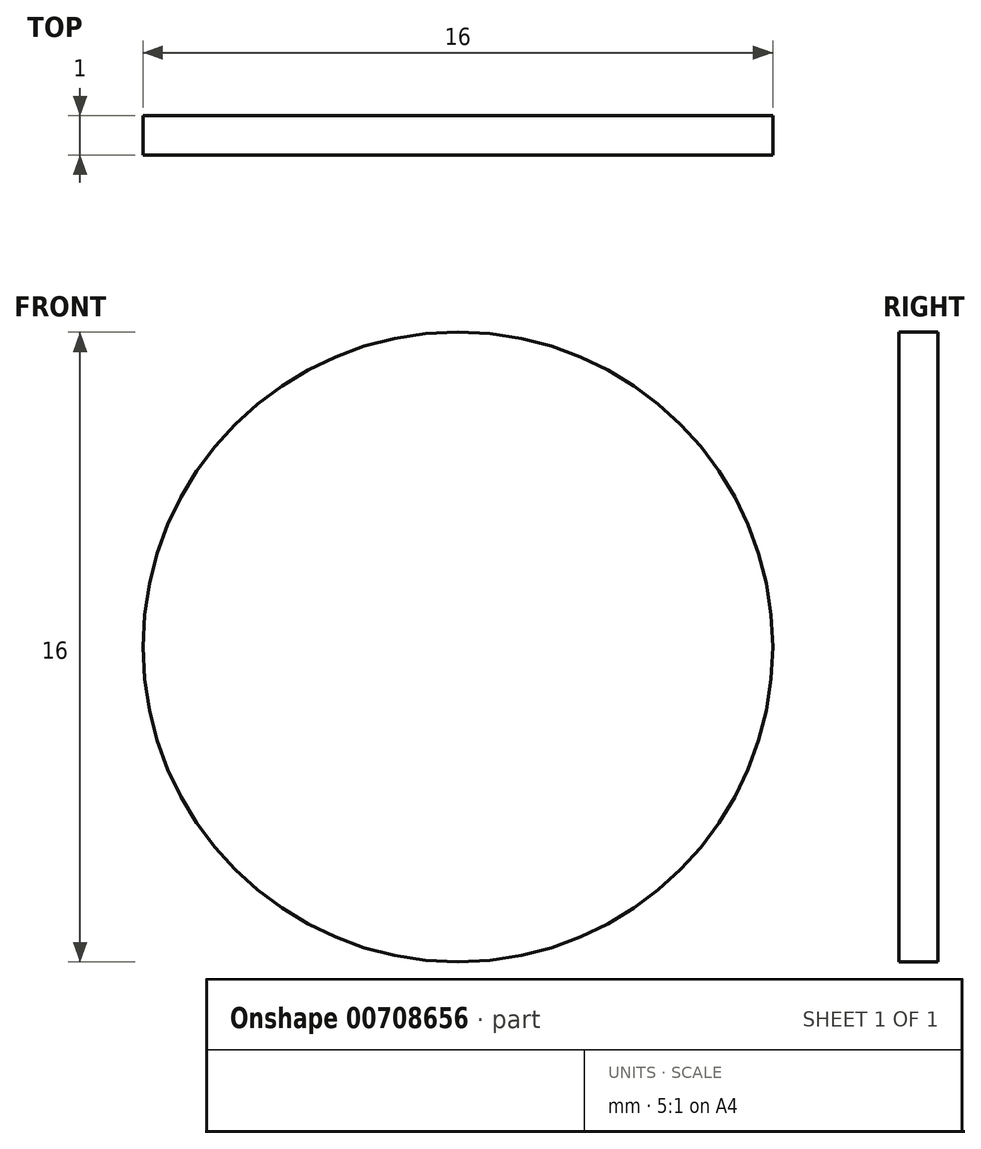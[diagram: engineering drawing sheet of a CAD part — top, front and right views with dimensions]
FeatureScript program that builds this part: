
annotation { "Feature Type Name" : "Feature", "Feature Type Description" : "" }
export const myFeature = defineFeature(function(context is Context, id is Id, definition is map)
    precondition{}
    {
        {
            var Q0;
            Q0=qCreatedBy(makeId("Front.planeOp"),FACE);
            var sketch = newSketch(context, id + "F0", { "sketchPlane" : qUnion([Q0])});
            skCircle(sketch, "E0", {"center": v(0, 0) * mm, "radius": 10 * mm});
            skCircle(sketch, "E1", {"center": v(0, 0) * mm, "radius": 8.5 * mm});
            skCircle(sketch, "E2", {"center": v(0, 0) * mm, "radius": 5.5 * mm});
            skCircle(sketch, "E3", {"center": v(0, 0) * mm, "radius": 2 * mm});
            skCircle(sketch, "E4", {"center": v(0, 0) * mm, "radius": 7 * mm});
            skCircle(sketch, "E5", {"center": v(0, 0) * mm, "radius": 3.5 * mm});
            skCircle(sketch, "E6", {"center": v(0, 0) * mm, "radius": 0.5 * mm});
            skSolve(sketch);
        }
        {
            var Q0;
            Q0=makeQuery(id+"F0.imprint","IMPRINT",FACE,{"disambiguationData":[TD([[makeQuery(id+"F0.imprint","IMPRINT",EDGE,{"derivedFrom":sQuery(id+"F0.wireOp",EDGE,"E6")}),1.0]])]});
            var sketch = newSketch(context, id + "F1", { "sketchPlane" : qUnion([Q0])});
            skCircle(sketch, "E7", {"center": v(0, 0) * mm, "radius": 8 * mm});
            skSolve(sketch);
        }
        {
            var Q0;
            Q0=qSketchRegion(id+"F1",true);
            extrude(context, id + "F2", {"entities" : qUnion([Q0]), "depth" : 1 * mm, "offsetDistance" : 25 * mm});
        }
    });
